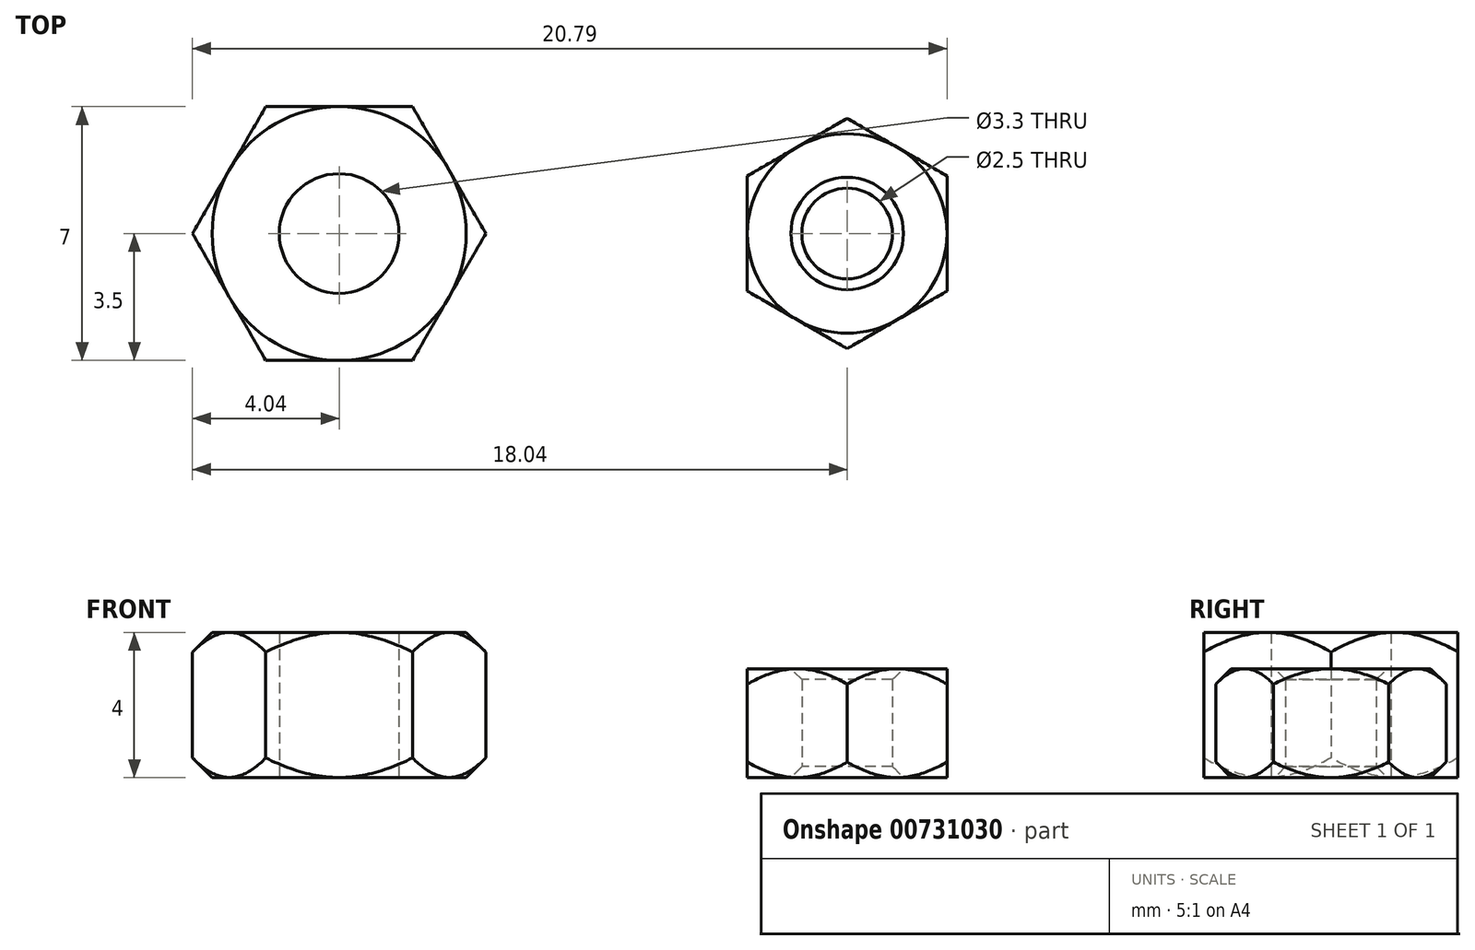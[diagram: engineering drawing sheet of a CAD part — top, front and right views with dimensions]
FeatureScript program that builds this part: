
annotation { "Feature Type Name" : "Feature", "Feature Type Description" : "" }
export const myFeature = defineFeature(function(context is Context, id is Id, definition is map)
    precondition{}
    {
        {
            var Q0;
            Q0=qCreatedBy(makeId("Top.planeOp"),FACE);
            var sketch = newSketch(context, id + "F0", { "sketchPlane" : qUnion([Q0])});
            skCircle(sketch, "E0.cCircle", {"center": v(0, 0) * mm, "radius": 2.75 * mm, "construction": true});
            skLineSegment(sketch, "E0.0", {"start": v(2.75, 1.59) * mm, "end": v(2.75, -1.59) * mm});
            skLineSegment(sketch, "E0.1", {"start": v(2.75, -1.59) * mm, "end": v(0, -3.18) * mm});
            skLineSegment(sketch, "E0.2", {"start": v(0, -3.18) * mm, "end": v(-2.75, -1.59) * mm});
            skLineSegment(sketch, "E0.3", {"start": v(-2.75, -1.59) * mm, "end": v(-2.75, 1.59) * mm});
            skLineSegment(sketch, "E0.4", {"start": v(-2.75, 1.59) * mm, "end": v(0, 3.18) * mm});
            skLineSegment(sketch, "E0.5", {"start": v(0, 3.18) * mm, "end": v(2.75, 1.59) * mm});
            skPoint(sketch, "E0.0.midPoint", {"position": v(2.75, 0) * mm});
            skCircle(sketch, "E1", {"center": v(0, 0) * mm, "radius": 1.25 * mm});
            skSolve(sketch);
        }
        {
            var Q0;
            Q0=makeQuery(id+"F0.imprint","IMPRINT",FACE,{"disambiguationData":[TD([[makeQuery(id+"F0.imprint","IMPRINT",EDGE,{"derivedFrom":sQuery(id+"F0.wireOp",EDGE,"E0.0")}),-1.0]])]});
            extrude(context, id + "F1", {"entities" : qUnion([Q0]), "depth" : 3 * mm, "offsetDistance" : 25 * mm});
        }
        {
            var Q0;
            Q0=makeQuery(id+"F1.opExtrude","CAP_EDGE",EDGE,{"disambiguationData":[OSD([sQuery(id+"F0.wireOp",EDGE,"E1")])],"isStart":false});
            var Q1;
            Q1=makeQuery(id+"F1.opExtrude","CAP_EDGE",EDGE,{"disambiguationData":[OSD([sQuery(id+"F0.wireOp",EDGE,"E1")])],"isStart":true});
            chamfer(context, id + "F2", {"entities" : qUnion([Q0, Q1]), "width" : 0.3 * mm, "tangentPropagation" : true});
        }
        {
            var Q0;
            Q0=qCreatedBy(makeId("Right.planeOp"),FACE);
            var sketch = newSketch(context, id + "F3", { "sketchPlane" : qUnion([Q0])});
            skLineSegment(sketch, "E2", {"start": v(2.75, 3) * mm, "end": v(3.18, 2.57) * mm});
            skLineSegment(sketch, "E3", {"start": v(3.18, 2.57) * mm, "end": v(3.18, 0.43) * mm});
            skLineSegment(sketch, "E4", {"start": v(3.18, 0.43) * mm, "end": v(2.75, 0) * mm});
            skLineSegment(sketch, "E5", {"start": v(2.75, 0) * mm, "end": v(3.98, 0) * mm});
            skLineSegment(sketch, "E6", {"start": v(3.98, 0) * mm, "end": v(3.98, 3) * mm});
            skLineSegment(sketch, "E7", {"start": v(3.98, 3) * mm, "end": v(2.75, 3) * mm});
            skLineSegment(sketch, "E8", {"start": v(0, 0) * mm, "end": v(0, 4.28) * mm, "construction": true});
            skSolve(sketch);
        }
        {
            var Q0;
            Q0=makeQuery(id+"F3.imprint","IMPRINT",FACE,{"disambiguationData":[TD([[makeQuery(id+"F3.imprint","IMPRINT",EDGE,{"derivedFrom":sQuery(id+"F3.wireOp",EDGE,"E2")}),1.0]])]});
            var Q1;
            Q1=sQuery(id+"F3.wireOp",EDGE,"E8");
            revolve(context, id + "F4", {"operationType" : NewBodyOperationType.REMOVE, "surfaceOperationType" : NewSurfaceOperationType.NEW, "entities" : qUnion([Q0]), "axis" : qUnion([Q1]), "revolveType" : RevolveType.FULL, "oppositeDirection" : true});
        }
        {
            var Q0;
            Q0=makeQuery(id+"F1.opExtrude","SWEPT_BODY",BODY,{"disambiguationData":[OSD([sQuery(id+"F0.wireOp",EDGE,"E0.0"),sQuery(id+"F0.wireOp",EDGE,"E0.1"),sQuery(id+"F0.wireOp",EDGE,"E0.2"),sQuery(id+"F0.wireOp",EDGE,"E0.3"),sQuery(id+"F0.wireOp",EDGE,"E0.4"),sQuery(id+"F0.wireOp",EDGE,"E0.5"),sQuery(id+"F0.wireOp",EDGE,"E1")])]});
            transform(context, id + "F5", {"entities" : qUnion([Q0]), "transformType" : TransformType.TRANSLATION_3D, "dx" : 32.8 * mm, "dy" : 0 * mm, "dz" : 0 * mm, "makeCopy" : false});
        }
        {
            var Q0;
            Q0=qCreatedBy(makeId("Top.planeOp"),FACE);
            var sketch = newSketch(context, id + "F6", { "sketchPlane" : qUnion([Q0])});
            skCircle(sketch, "E9", {"center": v(0, 0) * mm, "radius": 1.65 * mm});
            skCircle(sketch, "E10.cCircle", {"center": v(0, 0) * mm, "radius": 3.5 * mm, "construction": true});
            skLineSegment(sketch, "E10.0", {"start": v(4.04, 0) * mm, "end": v(2.02, -3.5) * mm});
            skLineSegment(sketch, "E10.1", {"start": v(2.02, -3.5) * mm, "end": v(-2.02, -3.5) * mm});
            skLineSegment(sketch, "E10.2", {"start": v(-2.02, -3.5) * mm, "end": v(-4.04, 0) * mm});
            skLineSegment(sketch, "E10.3", {"start": v(-4.04, 0) * mm, "end": v(-2.02, 3.5) * mm});
            skLineSegment(sketch, "E10.4", {"start": v(-2.02, 3.5) * mm, "end": v(2.02, 3.5) * mm});
            skLineSegment(sketch, "E10.5", {"start": v(2.02, 3.5) * mm, "end": v(4.04, 0) * mm});
            skPoint(sketch, "E10.0.midPoint", {"position": v(21.23, 2.64) * mm});
            skSolve(sketch);
        }
        {
            var Q0;
            Q0=makeQuery(id+"F6.imprint","IMPRINT",FACE,{"disambiguationData":[TD([[makeQuery(id+"F6.imprint","IMPRINT",EDGE,{"derivedFrom":sQuery(id+"F6.wireOp",EDGE,"E9")}),-1.0]])]});
            extrude(context, id + "F7", {"entities" : qUnion([Q0]), "depth" : 4 * mm, "offsetDistance" : 25 * mm});
        }
        {
            var Q0;
            Q0=qCreatedBy(makeId("Front.planeOp"),FACE);
            var sketch = newSketch(context, id + "F8", { "sketchPlane" : qUnion([Q0])});
            skLineSegment(sketch, "E11", {"start": v(3.5, 4) * mm, "end": v(4.04, 3.46) * mm});
            skLineSegment(sketch, "E12", {"start": v(4.04, 3.46) * mm, "end": v(4.04, 0.54) * mm});
            skLineSegment(sketch, "E13", {"start": v(4.04, 0.54) * mm, "end": v(3.5, 0) * mm});
            skLineSegment(sketch, "E14", {"start": v(3.5, 0) * mm, "end": v(5.04, 0) * mm});
            skLineSegment(sketch, "E15", {"start": v(5.04, 0) * mm, "end": v(5.04, 4) * mm});
            skLineSegment(sketch, "E16", {"start": v(5.04, 4) * mm, "end": v(3.5, 4) * mm});
            skLineSegment(sketch, "E17", {"start": v(0, 0) * mm, "end": v(0, 5.2) * mm, "construction": true});
            skSolve(sketch);
        }
        {
            var Q0;
            Q0=makeQuery(id+"F8.imprint","IMPRINT",FACE,{"disambiguationData":[TD([[makeQuery(id+"F8.imprint","IMPRINT",EDGE,{"derivedFrom":sQuery(id+"F8.wireOp",EDGE,"E11")}),1.0]])]});
            var Q1;
            Q1=makeQuery(id+"F7.opExtrude","SWEPT_FACE",FACE,{"disambiguationData":[OSD([sQuery(id+"F6.wireOp",EDGE,"E9")])]});
            revolve(context, id + "F9", {"operationType" : NewBodyOperationType.REMOVE, "surfaceOperationType" : NewSurfaceOperationType.NEW, "entities" : qUnion([Q0]), "axis" : qUnion([Q1]), "revolveType" : RevolveType.FULL, "oppositeDirection" : true});
        }
        {
            var Q0;
            Q0=makeQuery(id+"F1.opExtrude","SWEPT_BODY",BODY,{"disambiguationData":[OSD([sQuery(id+"F0.wireOp",EDGE,"E0.0"),sQuery(id+"F0.wireOp",EDGE,"E0.1"),sQuery(id+"F0.wireOp",EDGE,"E0.2"),sQuery(id+"F0.wireOp",EDGE,"E0.3"),sQuery(id+"F0.wireOp",EDGE,"E0.4"),sQuery(id+"F0.wireOp",EDGE,"E0.5"),sQuery(id+"F0.wireOp",EDGE,"E1")])]});
            transform(context, id + "F10", {"entities" : qUnion([Q0]), "transformType" : TransformType.TRANSLATION_3D, "dx" : 27 * mm, "dy" : 0 * mm, "dz" : 0 * mm, "makeCopy" : false});
        }
        {
            var Q0;
            Q0=makeQuery(id+"F7.opExtrude","SWEPT_BODY",BODY,{"disambiguationData":[OSD([sQuery(id+"F6.wireOp",EDGE,"E9"),sQuery(id+"F6.wireOp",EDGE,"E10.0"),sQuery(id+"F6.wireOp",EDGE,"E10.1"),sQuery(id+"F6.wireOp",EDGE,"E10.2"),sQuery(id+"F6.wireOp",EDGE,"E10.3"),sQuery(id+"F6.wireOp",EDGE,"E10.4"),sQuery(id+"F6.wireOp",EDGE,"E10.5")])]});
            transform(context, id + "F11", {"entities" : qUnion([Q0]), "transformType" : TransformType.TRANSLATION_3D, "dx" : 45.8 * mm, "dy" : 0 * mm, "dz" : 0 * mm, "makeCopy" : false});
        }
    });
